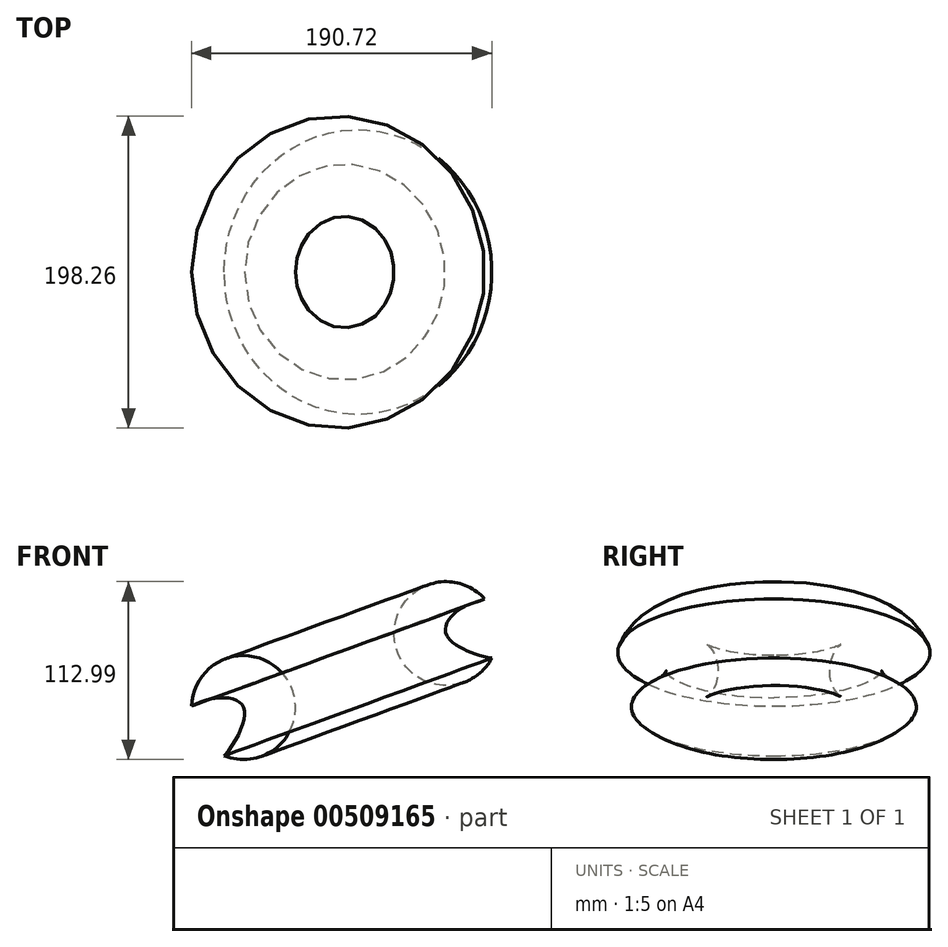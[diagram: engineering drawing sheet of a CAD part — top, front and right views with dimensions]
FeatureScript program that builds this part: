
annotation { "Feature Type Name" : "Feature", "Feature Type Description" : "" }
export const myFeature = defineFeature(function(context is Context, id is Id, definition is map)
    precondition{}
    {
        {
            var Q0;
            Q0=qCreatedBy(makeId("Front.planeOp"),FACE);
            var sketch = newSketch(context, id + "F0", { "sketchPlane" : qUnion([Q0])});
            skArc(sketch, "E0", {"start": v(24.62, 44.66) * mm, "mid": v(-32.78, 18.76) * mm, "end": v(29.1, 7.1) * mm});
            skFitSpline(sketch, "E1", {"points": [v(47.98, 62.5) * mm, v(47.04, 38.69) * mm, v(32.6, 44.88) * mm, v(0, 22.68) * mm, v(63.36, 14.2) * mm, v(47.98, 62.5) * mm]});
            skLineSegment(sketch, "E2", {"start": v(-40.9, 87.19) * mm, "end": v(-40.9, -64.92) * mm});
            skLineSegment(sketch, "E3", {"start": v(-40.9, -64.92) * mm, "end": v(-85.72, 57.83) * mm, "construction": true});
            skSolve(sketch);
        }
        {
            var Q0;
            Q0=makeQuery(id+"F0.imprint","IMPRINT",FACE,{"disambiguationData":[TD([[makeQuery(id+"F0.imprint","IMPRINT",EDGE,{"derivedFrom":sQuery(id+"F0.wireOp",EDGE,"E0")}),1.0]])]});
            var Q1;
            Q1=sQuery(id+"F0.wireOp",EDGE,"E3");
            revolve(context, id + "F1", {"entities" : qUnion([Q0]), "axis" : qUnion([Q1]), "revolveType" : RevolveType.FULL});
        }
    });
